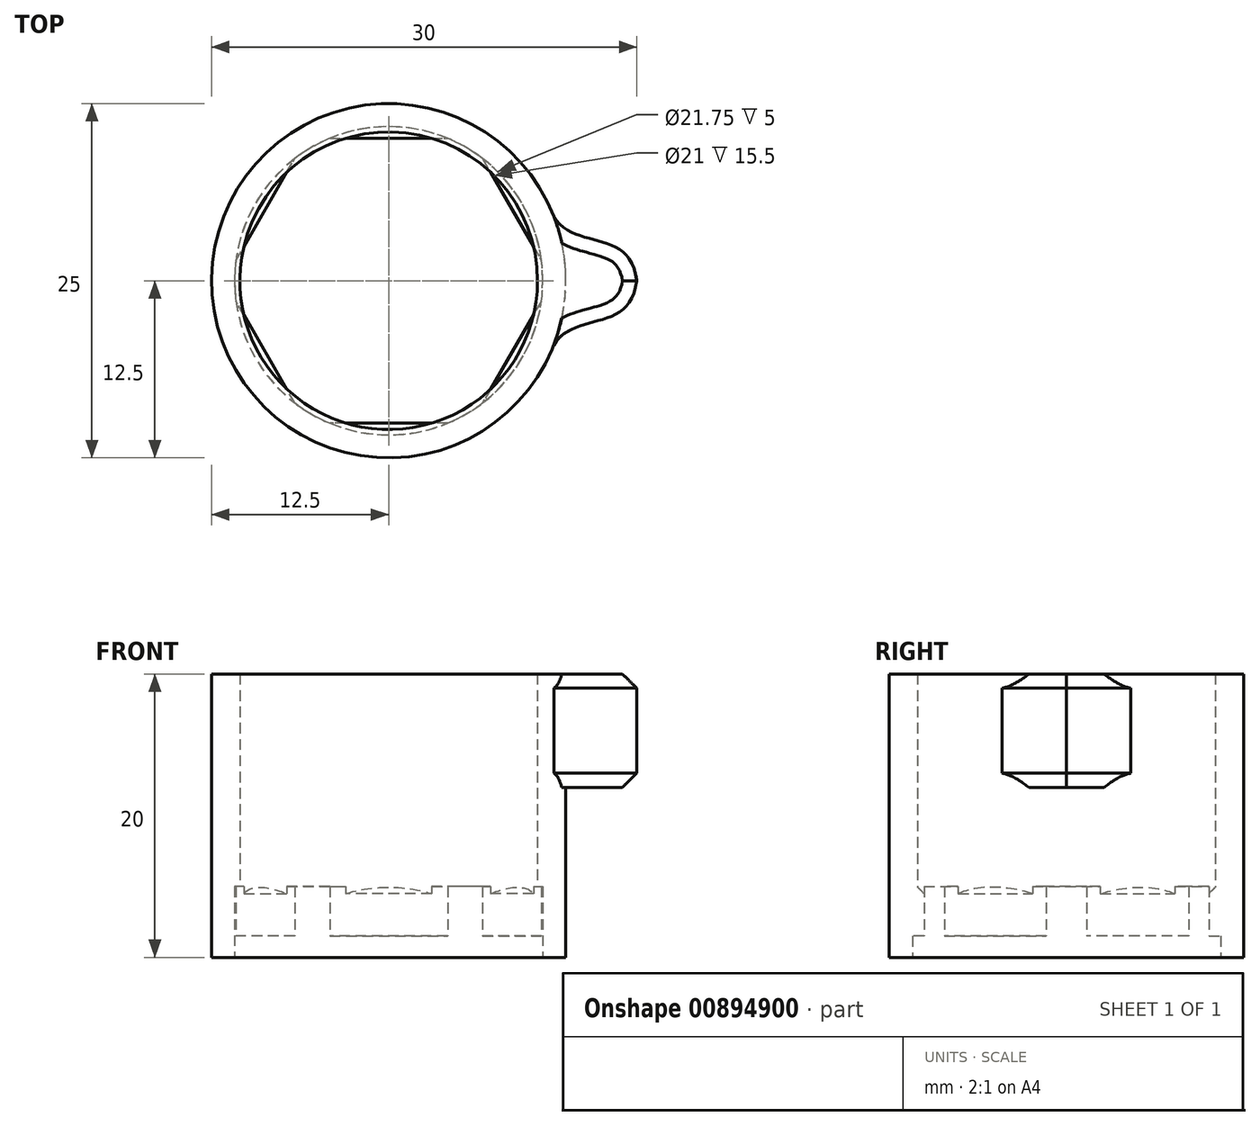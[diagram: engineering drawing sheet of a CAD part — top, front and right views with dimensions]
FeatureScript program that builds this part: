
annotation { "Feature Type Name" : "Feature", "Feature Type Description" : "" }
export const myFeature = defineFeature(function(context is Context, id is Id, definition is map)
    precondition{}
    {
        {
            var Q0;
            Q0=qCreatedBy(makeId("Top.planeOp"),FACE);
            var sketch = newSketch(context, id + "F0", { "sketchPlane" : qUnion([Q0])});
            skCircle(sketch, "E0.cCircle", {"center": v(0, 0) * mm, "radius": 10.05 * mm, "construction": true});
            skLineSegment(sketch, "E0.0", {"start": v(-5.8, 10.05) * mm, "end": v(5.8, 10.05) * mm});
            skLineSegment(sketch, "E0.1", {"start": v(5.8, 10.05) * mm, "end": v(11.6, 0) * mm});
            skLineSegment(sketch, "E0.2", {"start": v(11.6, 0) * mm, "end": v(5.8, -10.05) * mm});
            skLineSegment(sketch, "E0.3", {"start": v(5.8, -10.05) * mm, "end": v(-5.8, -10.05) * mm});
            skLineSegment(sketch, "E0.4", {"start": v(-5.8, -10.05) * mm, "end": v(-11.6, 0) * mm});
            skLineSegment(sketch, "E0.5", {"start": v(-11.6, 0) * mm, "end": v(-5.8, 10.05) * mm});
            skPoint(sketch, "E0.0.midPoint", {"position": v(0, 10.05) * mm});
            skCircle(sketch, "E1", {"center": v(0, 0) * mm, "radius": 10.88 * mm});
            skCircle(sketch, "E2", {"center": v(0, 0) * mm, "radius": 12.5 * mm});
            skSolve(sketch);
        }
        {
            var Q0;
            {var subQ0=sQuery(id+"F0.wireOp",EDGE,"E1");var subQ1=sQuery(id+"F0.wireOp",EDGE,"E0.0");var subQ2=makeQuery(id+"F0.imprint","INTERSECT",VERTEX,{"disambiguationData":[OD(0.0)],"derivedFrom":[subQ1,subQ0]});Q0=makeQuery(id+"F0.imprint","IMPRINT",FACE,{"disambiguationData":[TD([[makeQuery(id+"F0.imprint","IMPRINT",EDGE,{"disambiguationData":[TD([[subQ2,-1.0]])],"derivedFrom":subQ1}),1.0]])]});}
            var Q1;
            Q1=makeQuery(id+"F0.imprint","IMPRINT",FACE,{"disambiguationData":[TD([[makeQuery(id+"F0.imprint","IMPRINT",EDGE,{"derivedFrom":sQuery(id+"F0.wireOp",EDGE,"E2")}),1.0]])]});
            var Q2;
            {var subQ0=sQuery(id+"F0.wireOp",EDGE,"E0.1");var subQ1=sQuery(id+"F0.wireOp",EDGE,"E0.0");var subQ2=makeQuery(id+"F0.imprint","INTERSECT",VERTEX,{"derivedFrom":[subQ1,subQ0]});Q2=makeQuery(id+"F0.imprint","IMPRINT",FACE,{"disambiguationData":[TD([[makeQuery(id+"F0.imprint","IMPRINT",EDGE,{"disambiguationData":[TD([[subQ2,1.0]])],"derivedFrom":subQ1}),-1.0]])]});}
            var Q3;
            {var subQ0=sQuery(id+"F0.wireOp",EDGE,"E1");var subQ1=sQuery(id+"F0.wireOp",EDGE,"E0.1");var subQ2=makeQuery(id+"F0.imprint","INTERSECT",VERTEX,{"disambiguationData":[OD(0.0)],"derivedFrom":[subQ1,subQ0]});Q3=makeQuery(id+"F0.imprint","IMPRINT",FACE,{"disambiguationData":[TD([[makeQuery(id+"F0.imprint","IMPRINT",EDGE,{"disambiguationData":[TD([[subQ2,-1.0]])],"derivedFrom":subQ1}),1.0]])]});}
            var Q4;
            {var subQ0=sQuery(id+"F0.wireOp",EDGE,"E0.2");var subQ1=sQuery(id+"F0.wireOp",EDGE,"E0.1");var subQ2=makeQuery(id+"F0.imprint","INTERSECT",VERTEX,{"derivedFrom":[subQ1,subQ0]});Q4=makeQuery(id+"F0.imprint","IMPRINT",FACE,{"disambiguationData":[TD([[makeQuery(id+"F0.imprint","IMPRINT",EDGE,{"disambiguationData":[TD([[subQ2,1.0]])],"derivedFrom":subQ1}),-1.0]])]});}
            var Q5;
            {var subQ0=sQuery(id+"F0.wireOp",EDGE,"E1");var subQ1=sQuery(id+"F0.wireOp",EDGE,"E0.2");var subQ2=makeQuery(id+"F0.imprint","INTERSECT",VERTEX,{"disambiguationData":[OD(0.0)],"derivedFrom":[subQ1,subQ0]});Q5=makeQuery(id+"F0.imprint","IMPRINT",FACE,{"disambiguationData":[TD([[makeQuery(id+"F0.imprint","IMPRINT",EDGE,{"disambiguationData":[TD([[subQ2,-1.0]])],"derivedFrom":subQ1}),1.0]])]});}
            var Q6;
            {var subQ0=sQuery(id+"F0.wireOp",EDGE,"E0.3");var subQ1=sQuery(id+"F0.wireOp",EDGE,"E0.2");var subQ2=makeQuery(id+"F0.imprint","INTERSECT",VERTEX,{"derivedFrom":[subQ1,subQ0]});Q6=makeQuery(id+"F0.imprint","IMPRINT",FACE,{"disambiguationData":[TD([[makeQuery(id+"F0.imprint","IMPRINT",EDGE,{"disambiguationData":[TD([[subQ2,1.0]])],"derivedFrom":subQ1}),-1.0]])]});}
            var Q7;
            {var subQ0=sQuery(id+"F0.wireOp",EDGE,"E1");var subQ1=sQuery(id+"F0.wireOp",EDGE,"E0.3");var subQ2=makeQuery(id+"F0.imprint","INTERSECT",VERTEX,{"disambiguationData":[OD(0.0)],"derivedFrom":[subQ1,subQ0]});Q7=makeQuery(id+"F0.imprint","IMPRINT",FACE,{"disambiguationData":[TD([[makeQuery(id+"F0.imprint","IMPRINT",EDGE,{"disambiguationData":[TD([[subQ2,-1.0]])],"derivedFrom":subQ1}),1.0]])]});}
            var Q8;
            {var subQ0=sQuery(id+"F0.wireOp",EDGE,"E0.4");var subQ1=sQuery(id+"F0.wireOp",EDGE,"E0.3");var subQ2=makeQuery(id+"F0.imprint","INTERSECT",VERTEX,{"derivedFrom":[subQ1,subQ0]});Q8=makeQuery(id+"F0.imprint","IMPRINT",FACE,{"disambiguationData":[TD([[makeQuery(id+"F0.imprint","IMPRINT",EDGE,{"disambiguationData":[TD([[subQ2,1.0]])],"derivedFrom":subQ1}),-1.0]])]});}
            var Q9;
            {var subQ0=sQuery(id+"F0.wireOp",EDGE,"E1");var subQ1=sQuery(id+"F0.wireOp",EDGE,"E0.4");var subQ2=makeQuery(id+"F0.imprint","INTERSECT",VERTEX,{"disambiguationData":[OD(0.0)],"derivedFrom":[subQ1,subQ0]});Q9=makeQuery(id+"F0.imprint","IMPRINT",FACE,{"disambiguationData":[TD([[makeQuery(id+"F0.imprint","IMPRINT",EDGE,{"disambiguationData":[TD([[subQ2,-1.0]])],"derivedFrom":subQ1}),1.0]])]});}
            var Q10;
            {var subQ0=sQuery(id+"F0.wireOp",EDGE,"E0.5");var subQ1=sQuery(id+"F0.wireOp",EDGE,"E0.4");var subQ2=makeQuery(id+"F0.imprint","INTERSECT",VERTEX,{"derivedFrom":[subQ1,subQ0]});Q10=makeQuery(id+"F0.imprint","IMPRINT",FACE,{"disambiguationData":[TD([[makeQuery(id+"F0.imprint","IMPRINT",EDGE,{"disambiguationData":[TD([[subQ2,1.0]])],"derivedFrom":subQ1}),-1.0]])]});}
            var Q11;
            {var subQ0=sQuery(id+"F0.wireOp",EDGE,"E1");var subQ1=sQuery(id+"F0.wireOp",EDGE,"E0.5");var subQ2=makeQuery(id+"F0.imprint","INTERSECT",VERTEX,{"disambiguationData":[OD(0.0)],"derivedFrom":[subQ1,subQ0]});Q11=makeQuery(id+"F0.imprint","IMPRINT",FACE,{"disambiguationData":[TD([[makeQuery(id+"F0.imprint","IMPRINT",EDGE,{"disambiguationData":[TD([[subQ2,-1.0]])],"derivedFrom":subQ1}),1.0]])]});}
            var Q12;
            {var subQ0=sQuery(id+"F0.wireOp",EDGE,"E0.5");var subQ1=sQuery(id+"F0.wireOp",EDGE,"E0.0");var subQ2=makeQuery(id+"F0.imprint","INTERSECT",VERTEX,{"derivedFrom":[subQ1,subQ0]});Q12=makeQuery(id+"F0.imprint","IMPRINT",FACE,{"disambiguationData":[TD([[makeQuery(id+"F0.imprint","IMPRINT",EDGE,{"disambiguationData":[TD([[subQ2,-1.0]])],"derivedFrom":subQ1}),-1.0]])]});}
            extrude(context, id + "F1", {"entities" : qUnion([Q0, Q1, Q2, Q3, Q4, Q5, Q6, Q7, Q8, Q9, Q10, Q11, Q12]), "depth" : 5 * mm, "offsetDistance" : 25 * mm});
        }
        {
            var Q0;
            {var subQ0=sQuery(id+"F0.wireOp",EDGE,"E1");var subQ1=sQuery(id+"F0.wireOp",EDGE,"E0.3");var subQ2=makeQuery(id+"F0.imprint","INTERSECT",VERTEX,{"disambiguationData":[OD(0.0)],"derivedFrom":[subQ1,subQ0]});Q0=makeQuery(id+"F0.imprint","IMPRINT",FACE,{"disambiguationData":[TD([[makeQuery(id+"F0.imprint","IMPRINT",EDGE,{"disambiguationData":[TD([[subQ2,-1.0]])],"derivedFrom":subQ1}),1.0]])]});}
            var Q1;
            {var subQ0=sQuery(id+"F0.wireOp",EDGE,"E1");var subQ1=sQuery(id+"F0.wireOp",EDGE,"E0.4");var subQ2=makeQuery(id+"F0.imprint","INTERSECT",VERTEX,{"disambiguationData":[OD(0.0)],"derivedFrom":[subQ1,subQ0]});Q1=makeQuery(id+"F0.imprint","IMPRINT",FACE,{"disambiguationData":[TD([[makeQuery(id+"F0.imprint","IMPRINT",EDGE,{"disambiguationData":[TD([[subQ2,-1.0]])],"derivedFrom":subQ1}),1.0]])]});}
            var Q2;
            {var subQ0=sQuery(id+"F0.wireOp",EDGE,"E1");var subQ1=sQuery(id+"F0.wireOp",EDGE,"E0.5");var subQ2=makeQuery(id+"F0.imprint","INTERSECT",VERTEX,{"disambiguationData":[OD(0.0)],"derivedFrom":[subQ1,subQ0]});Q2=makeQuery(id+"F0.imprint","IMPRINT",FACE,{"disambiguationData":[TD([[makeQuery(id+"F0.imprint","IMPRINT",EDGE,{"disambiguationData":[TD([[subQ2,-1.0]])],"derivedFrom":subQ1}),1.0]])]});}
            var Q3;
            {var subQ0=sQuery(id+"F0.wireOp",EDGE,"E1");var subQ1=sQuery(id+"F0.wireOp",EDGE,"E0.0");var subQ2=makeQuery(id+"F0.imprint","INTERSECT",VERTEX,{"disambiguationData":[OD(0.0)],"derivedFrom":[subQ1,subQ0]});Q3=makeQuery(id+"F0.imprint","IMPRINT",FACE,{"disambiguationData":[TD([[makeQuery(id+"F0.imprint","IMPRINT",EDGE,{"disambiguationData":[TD([[subQ2,-1.0]])],"derivedFrom":subQ1}),1.0]])]});}
            var Q4;
            {var subQ0=sQuery(id+"F0.wireOp",EDGE,"E1");var subQ1=sQuery(id+"F0.wireOp",EDGE,"E0.1");var subQ2=makeQuery(id+"F0.imprint","INTERSECT",VERTEX,{"disambiguationData":[OD(0.0)],"derivedFrom":[subQ1,subQ0]});Q4=makeQuery(id+"F0.imprint","IMPRINT",FACE,{"disambiguationData":[TD([[makeQuery(id+"F0.imprint","IMPRINT",EDGE,{"disambiguationData":[TD([[subQ2,-1.0]])],"derivedFrom":subQ1}),1.0]])]});}
            var Q5;
            {var subQ0=sQuery(id+"F0.wireOp",EDGE,"E1");var subQ1=sQuery(id+"F0.wireOp",EDGE,"E0.2");var subQ2=makeQuery(id+"F0.imprint","INTERSECT",VERTEX,{"disambiguationData":[OD(0.0)],"derivedFrom":[subQ1,subQ0]});Q5=makeQuery(id+"F0.imprint","IMPRINT",FACE,{"disambiguationData":[TD([[makeQuery(id+"F0.imprint","IMPRINT",EDGE,{"disambiguationData":[TD([[subQ2,-1.0]])],"derivedFrom":subQ1}),1.0]])]});}
            extrude(context, id + "F2", {"entities" : qUnion([Q0, Q1, Q2, Q3, Q4, Q5]), "operationType" : NewBodyOperationType.REMOVE, "depth" : 1.5 * mm, "offsetDistance" : 25 * mm});
        }
        {
            var Q0;
            Q0=makeQuery(id+"F1.opExtrude","CAP_FACE",FACE,{"disambiguationData":[OSD([sQuery(id+"F0.wireOp",EDGE,"E0.0"),sQuery(id+"F0.wireOp",EDGE,"E0.1"),sQuery(id+"F0.wireOp",EDGE,"E0.2"),sQuery(id+"F0.wireOp",EDGE,"E0.3"),sQuery(id+"F0.wireOp",EDGE,"E0.4"),sQuery(id+"F0.wireOp",EDGE,"E0.5"),sQuery(id+"F0.wireOp",EDGE,"E1"),sQuery(id+"F0.wireOp",EDGE,"E2")])],"isStart":false});
            var sketch = newSketch(context, id + "F3", { "sketchPlane" : qUnion([Q0])});
            skCircle(sketch, "E3", {"center": v(0, 0) * mm, "radius": 10.5 * mm});
            skCircle(sketch, "E4.0", {"center": v(0, 0) * mm, "radius": 12.5 * mm});
            skSolve(sketch);
        }
        {
            var Q0;
            {var subQ1=sQuery(id+"F0.wireOp",EDGE,"E0.0");var subQ7=sQuery(id+"F0.wireOp",EDGE,"E1");var subQ8=makeQuery(id+"F1.opExtrude","CAP_EDGE",EDGE,{"disambiguationData":[OSD([subQ7]),TDD([makeQuery(id+"F0.imprint","IMPRINT",EDGE,{"disambiguationData":[TD([[makeQuery(id+"F0.imprint","INTERSECT",VERTEX,{"disambiguationData":[OD(0.0)],"derivedFrom":[subQ1,subQ7]}),-1.0]])],"derivedFrom":subQ7})])],"isStart":false});Q0=makeQuery(id+"F3.imprint","IMPRINT",FACE,{"disambiguationData":[TD([[makeQuery(id+"F3.imprint","IMPRINT",EDGE,{"derivedFrom":subQ8}),1.0]])]});}
            var Q1;
            {var subQ4=sQuery(id+"F0.wireOp",EDGE,"E0.0");var subQ7=sQuery(id+"F0.wireOp",EDGE,"E1");var subQ8=makeQuery(id+"F1.opExtrude","CAP_EDGE",EDGE,{"disambiguationData":[OSD([subQ7]),TDD([makeQuery(id+"F0.imprint","IMPRINT",EDGE,{"disambiguationData":[TD([[makeQuery(id+"F0.imprint","INTERSECT",VERTEX,{"disambiguationData":[OD(1.0)],"derivedFrom":[subQ4,subQ7]}),1.0]])],"derivedFrom":subQ7})])],"isStart":false});Q1=makeQuery(id+"F3.imprint","IMPRINT",FACE,{"disambiguationData":[TD([[makeQuery(id+"F3.imprint","IMPRINT",EDGE,{"derivedFrom":subQ8}),1.0]])]});}
            var Q2;
            {var subQ1=sQuery(id+"F0.wireOp",EDGE,"E0.1");var subQ7=sQuery(id+"F0.wireOp",EDGE,"E1");var subQ8=makeQuery(id+"F1.opExtrude","CAP_EDGE",EDGE,{"disambiguationData":[OSD([subQ7]),TDD([makeQuery(id+"F0.imprint","IMPRINT",EDGE,{"disambiguationData":[TD([[makeQuery(id+"F0.imprint","INTERSECT",VERTEX,{"disambiguationData":[OD(1.0)],"derivedFrom":[subQ1,subQ7]}),1.0]])],"derivedFrom":subQ7})])],"isStart":false});Q2=makeQuery(id+"F3.imprint","IMPRINT",FACE,{"disambiguationData":[TD([[makeQuery(id+"F3.imprint","IMPRINT",EDGE,{"derivedFrom":subQ8}),1.0]])]});}
            var Q3;
            {var subQ4=sQuery(id+"F0.wireOp",EDGE,"E0.2");var subQ7=sQuery(id+"F0.wireOp",EDGE,"E1");var subQ8=makeQuery(id+"F1.opExtrude","CAP_EDGE",EDGE,{"disambiguationData":[OSD([subQ7]),TDD([makeQuery(id+"F0.imprint","IMPRINT",EDGE,{"disambiguationData":[TD([[makeQuery(id+"F0.imprint","INTERSECT",VERTEX,{"disambiguationData":[OD(1.0)],"derivedFrom":[subQ4,subQ7]}),1.0]])],"derivedFrom":subQ7})])],"isStart":false});Q3=makeQuery(id+"F3.imprint","IMPRINT",FACE,{"disambiguationData":[TD([[makeQuery(id+"F3.imprint","IMPRINT",EDGE,{"derivedFrom":subQ8}),1.0]])]});}
            var Q4;
            {var subQ4=sQuery(id+"F0.wireOp",EDGE,"E0.3");var subQ7=sQuery(id+"F0.wireOp",EDGE,"E1");var subQ8=makeQuery(id+"F1.opExtrude","CAP_EDGE",EDGE,{"disambiguationData":[OSD([subQ7]),TDD([makeQuery(id+"F0.imprint","IMPRINT",EDGE,{"disambiguationData":[TD([[makeQuery(id+"F0.imprint","INTERSECT",VERTEX,{"disambiguationData":[OD(1.0)],"derivedFrom":[subQ4,subQ7]}),1.0]])],"derivedFrom":subQ7})])],"isStart":false});Q4=makeQuery(id+"F3.imprint","IMPRINT",FACE,{"disambiguationData":[TD([[makeQuery(id+"F3.imprint","IMPRINT",EDGE,{"derivedFrom":subQ8}),1.0]])]});}
            var Q5;
            {var subQ4=sQuery(id+"F0.wireOp",EDGE,"E0.4");var subQ7=sQuery(id+"F0.wireOp",EDGE,"E1");var subQ8=makeQuery(id+"F1.opExtrude","CAP_EDGE",EDGE,{"disambiguationData":[OSD([subQ7]),TDD([makeQuery(id+"F0.imprint","IMPRINT",EDGE,{"disambiguationData":[TD([[makeQuery(id+"F0.imprint","INTERSECT",VERTEX,{"disambiguationData":[OD(1.0)],"derivedFrom":[subQ4,subQ7]}),1.0]])],"derivedFrom":subQ7})])],"isStart":false});Q5=makeQuery(id+"F3.imprint","IMPRINT",FACE,{"disambiguationData":[TD([[makeQuery(id+"F3.imprint","IMPRINT",EDGE,{"derivedFrom":subQ8}),1.0]])]});}
            var Q6;
            Q6=makeQuery(id+"F3.imprint","IMPRINT",FACE,{"disambiguationData":[TD([[makeQuery(id+"F3.imprint","IMPRINT",EDGE,{"derivedFrom":sQuery(id+"F3.wireOp",EDGE,"E4.0")}),1.0]])]});
            extrude(context, id + "F4", {"entities" : qUnion([Q0, Q1, Q2, Q3, Q4, Q5, Q6]), "operationType" : NewBodyOperationType.ADD, "depth" : 15 * mm, "offsetDistance" : 25 * mm});
        }
        {
            var Q0;
            Q0=makeQuery(id+"F4.opExtrude","CAP_FACE",FACE,{"disambiguationData":[OSD([sQuery(id+"F3.wireOp",EDGE,"E3"),sQuery(id+"F3.wireOp",EDGE,"E4.0")])],"isStart":false});
            var sketch = newSketch(context, id + "F5", { "sketchPlane" : qUnion([Q0])});
            skCircle(sketch, "E5", {"center": v(0, 0) * mm, "radius": 17.5 * mm});
            skLineSegment(sketch, "E6", {"start": v(17.5, 0) * mm, "end": v(12.5, 0) * mm, "construction": true});
            skLineSegment(sketch, "E7", {"start": v(15.86, 7.4) * mm, "end": v(11.33, 5.28) * mm, "construction": true});
            skFitSpline(sketch, "E8", {"points": [v(17.5, 0) * mm, v(11.33, 5.28) * mm], "startDerivative": vector(-1.48, 12.4) * mm, "endDerivative": vector(-3.15, 10.62) * mm});
            skFitSpline(sketch, "E9.MirrorCS", {"points": [v(17.5, 0) * mm, v(11.33, -5.28) * mm], "startDerivative": vector(-1.48, -12.4) * mm, "endDerivative": vector(-3.15, -10.62) * mm});
            skSolve(sketch);
        }
        {
            var Q0;
            {var subQ1=sQuery(id+"F5.wireOp",EDGE,"E8");var subQ3=makeQuery(id+"F4.opExtrude","CAP_EDGE",EDGE,{"disambiguationData":[OSD([sQuery(id+"F3.wireOp",EDGE,"E4.0")])],"isStart":false});var subQ4=makeQuery(id+"F5.imprint","INTERSECT",VERTEX,{"disambiguationData":[OD(1.0)],"derivedFrom":[subQ3,subQ1]});Q0=makeQuery(id+"F5.imprint","IMPRINT",FACE,{"disambiguationData":[TD([[makeQuery(id+"F5.imprint","IMPRINT",EDGE,{"disambiguationData":[TD([[subQ4,1.0]])],"derivedFrom":subQ3}),-1.0]])]});}
            extrude(context, id + "F6", {"entities" : qUnion([Q0]), "operationType" : NewBodyOperationType.ADD, "oppositeDirection" : true, "depth" : 8 * mm, "offsetDistance" : 25 * mm});
        }
        {
            var Q0;
            Q0=makeQuery(id+"F6.opExtrude","CAP_EDGE",EDGE,{"disambiguationData":[OSD([sQuery(id+"F5.wireOp",EDGE,"E9.MirrorCS")])],"isStart":false});
            var Q1;
            Q1=makeQuery(id+"F6.opExtrude","CAP_EDGE",EDGE,{"disambiguationData":[OSD([sQuery(id+"F5.wireOp",EDGE,"E8")])],"isStart":false});
            var Q2;
            Q2=makeQuery(id+"F6.opExtrude","CAP_EDGE",EDGE,{"disambiguationData":[OSD([sQuery(id+"F5.wireOp",EDGE,"E9.MirrorCS")])],"isStart":true});
            var Q3;
            Q3=makeQuery(id+"F6.opExtrude","CAP_EDGE",EDGE,{"disambiguationData":[OSD([sQuery(id+"F5.wireOp",EDGE,"E8")])],"isStart":true});
            chamfer(context, id + "F7", {"entities" : qUnion([Q0, Q1, Q2, Q3]), "width" : 1 * mm, "tangentPropagation" : true});
        }
        {
            var Q0;
            {var subQ0=sQuery(id+"F0.wireOp",EDGE,"E0.5");Q0=makeQuery(id+"F4.boolean.opBoolean","SPLIT",EDGE,{"disambiguationData":[topologyDisambiguationEdgeConnected([makeQuery(id+"F1.opExtrude","CAP_FACE",FACE,{"disambiguationData":[OSD([sQuery(id+"F0.wireOp",EDGE,"E0.0"),sQuery(id+"F0.wireOp",EDGE,"E0.1"),sQuery(id+"F0.wireOp",EDGE,"E0.2"),sQuery(id+"F0.wireOp",EDGE,"E0.3"),sQuery(id+"F0.wireOp",EDGE,"E0.4"),subQ0,sQuery(id+"F0.wireOp",EDGE,"E1"),sQuery(id+"F0.wireOp",EDGE,"E2")])],"isStart":false}),makeQuery(id+"F1.opExtrude","SWEPT_FACE",FACE,{"disambiguationData":[OSD([subQ0])]})])],"derivedFrom":makeQuery(id+"F1.opExtrude","CAP_EDGE",EDGE,{"disambiguationData":[OSD([subQ0])],"isStart":false})});}
            var Q1;
            {var subQ0=sQuery(id+"F0.wireOp",EDGE,"E0.4");Q1=makeQuery(id+"F4.boolean.opBoolean","SPLIT",EDGE,{"disambiguationData":[topologyDisambiguationEdgeConnected([makeQuery(id+"F1.opExtrude","CAP_FACE",FACE,{"disambiguationData":[OSD([sQuery(id+"F0.wireOp",EDGE,"E0.0"),sQuery(id+"F0.wireOp",EDGE,"E0.1"),sQuery(id+"F0.wireOp",EDGE,"E0.2"),sQuery(id+"F0.wireOp",EDGE,"E0.3"),subQ0,sQuery(id+"F0.wireOp",EDGE,"E0.5"),sQuery(id+"F0.wireOp",EDGE,"E1"),sQuery(id+"F0.wireOp",EDGE,"E2")])],"isStart":false}),makeQuery(id+"F1.opExtrude","SWEPT_FACE",FACE,{"disambiguationData":[OSD([subQ0])]})])],"derivedFrom":makeQuery(id+"F1.opExtrude","CAP_EDGE",EDGE,{"disambiguationData":[OSD([subQ0])],"isStart":false})});}
            var Q2;
            {var subQ0=sQuery(id+"F0.wireOp",EDGE,"E0.0");Q2=makeQuery(id+"F4.boolean.opBoolean","SPLIT",EDGE,{"disambiguationData":[topologyDisambiguationEdgeConnected([makeQuery(id+"F1.opExtrude","SWEPT_FACE",FACE,{"disambiguationData":[OSD([subQ0])]}),makeQuery(id+"F1.opExtrude","CAP_FACE",FACE,{"disambiguationData":[OSD([subQ0,sQuery(id+"F0.wireOp",EDGE,"E0.1"),sQuery(id+"F0.wireOp",EDGE,"E0.2"),sQuery(id+"F0.wireOp",EDGE,"E0.3"),sQuery(id+"F0.wireOp",EDGE,"E0.4"),sQuery(id+"F0.wireOp",EDGE,"E0.5"),sQuery(id+"F0.wireOp",EDGE,"E1"),sQuery(id+"F0.wireOp",EDGE,"E2")])],"isStart":false})])],"derivedFrom":makeQuery(id+"F1.opExtrude","CAP_EDGE",EDGE,{"disambiguationData":[OSD([subQ0])],"isStart":false})});}
            var Q3;
            {var subQ0=sQuery(id+"F0.wireOp",EDGE,"E0.1");Q3=makeQuery(id+"F4.boolean.opBoolean","SPLIT",EDGE,{"disambiguationData":[topologyDisambiguationEdgeConnected([makeQuery(id+"F1.opExtrude","CAP_FACE",FACE,{"disambiguationData":[OSD([sQuery(id+"F0.wireOp",EDGE,"E0.0"),subQ0,sQuery(id+"F0.wireOp",EDGE,"E0.2"),sQuery(id+"F0.wireOp",EDGE,"E0.3"),sQuery(id+"F0.wireOp",EDGE,"E0.4"),sQuery(id+"F0.wireOp",EDGE,"E0.5"),sQuery(id+"F0.wireOp",EDGE,"E1"),sQuery(id+"F0.wireOp",EDGE,"E2")])],"isStart":false}),makeQuery(id+"F1.opExtrude","SWEPT_FACE",FACE,{"disambiguationData":[OSD([subQ0])]})])],"derivedFrom":makeQuery(id+"F1.opExtrude","CAP_EDGE",EDGE,{"disambiguationData":[OSD([subQ0])],"isStart":false})});}
            var Q4;
            {var subQ0=sQuery(id+"F0.wireOp",EDGE,"E0.2");Q4=makeQuery(id+"F4.boolean.opBoolean","SPLIT",EDGE,{"disambiguationData":[topologyDisambiguationEdgeConnected([makeQuery(id+"F1.opExtrude","CAP_FACE",FACE,{"disambiguationData":[OSD([sQuery(id+"F0.wireOp",EDGE,"E0.0"),sQuery(id+"F0.wireOp",EDGE,"E0.1"),subQ0,sQuery(id+"F0.wireOp",EDGE,"E0.3"),sQuery(id+"F0.wireOp",EDGE,"E0.4"),sQuery(id+"F0.wireOp",EDGE,"E0.5"),sQuery(id+"F0.wireOp",EDGE,"E1"),sQuery(id+"F0.wireOp",EDGE,"E2")])],"isStart":false}),makeQuery(id+"F1.opExtrude","SWEPT_FACE",FACE,{"disambiguationData":[OSD([subQ0])]})])],"derivedFrom":makeQuery(id+"F1.opExtrude","CAP_EDGE",EDGE,{"disambiguationData":[OSD([subQ0])],"isStart":false})});}
            var Q5;
            {var subQ0=sQuery(id+"F0.wireOp",EDGE,"E0.3");Q5=makeQuery(id+"F4.boolean.opBoolean","SPLIT",EDGE,{"disambiguationData":[topologyDisambiguationEdgeConnected([makeQuery(id+"F1.opExtrude","CAP_FACE",FACE,{"disambiguationData":[OSD([sQuery(id+"F0.wireOp",EDGE,"E0.0"),sQuery(id+"F0.wireOp",EDGE,"E0.1"),sQuery(id+"F0.wireOp",EDGE,"E0.2"),subQ0,sQuery(id+"F0.wireOp",EDGE,"E0.4"),sQuery(id+"F0.wireOp",EDGE,"E0.5"),sQuery(id+"F0.wireOp",EDGE,"E1"),sQuery(id+"F0.wireOp",EDGE,"E2")])],"isStart":false}),makeQuery(id+"F1.opExtrude","SWEPT_FACE",FACE,{"disambiguationData":[OSD([subQ0])]})])],"derivedFrom":makeQuery(id+"F1.opExtrude","CAP_EDGE",EDGE,{"disambiguationData":[OSD([subQ0])],"isStart":false})});}
            chamfer(context, id + "F8", {"entities" : qUnion([Q0, Q1, Q2, Q3, Q4, Q5]), "width" : .5 * mm, "tangentPropagation" : true});
        }
    });
